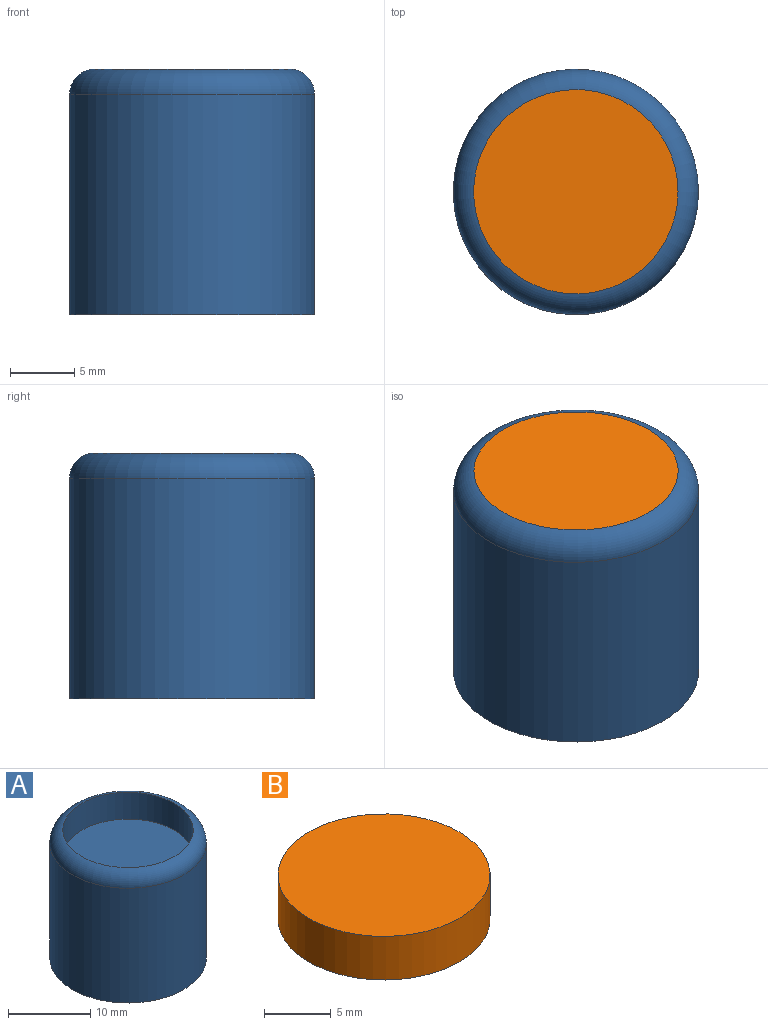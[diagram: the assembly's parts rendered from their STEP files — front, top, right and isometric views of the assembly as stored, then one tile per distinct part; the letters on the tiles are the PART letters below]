
ASSEMBLY  parts=2 mates=1
PART A: 5 faces, bbox 20.6x20.6x19.1 mm
  f0: cylinder r=9.53mm len=19.05mm, axis (0,0,-1), area 1023mm2, adj f1,f4
  f1: plane 19.05x19.05mm, normal (0,0,-1), area 285mm2, adj f0
  f2: cylinder r=7.94mm len=15.88mm, axis (0,0,1), area 199.5mm2, adj f3,f4
  f3: plane 15.88x15.88mm, normal (0,0,1), area 197.9mm2, adj f2
  f4: torus R=7.52mm, axis (0,0,1), area 153.5mm2, adj f0,f2
PART B: 3 faces, bbox 15.9x15.9x4 mm
  f0: plane 15.88x15.88mm, normal (0,0,-1), area 197.9mm2, adj f1
  f1: cylinder r=7.94mm len=15.88mm, axis (0,0,1), area 199.5mm2, adj f0,f2
  f2: plane 15.88x15.88mm, normal (0,0,1), area 197.9mm2, adj f1
PLACE A at identity
PLACE B at identity
MATE fastened B.f1 <-> A.f2  axis (0,0,-1) through (0,0,15.05)mm
